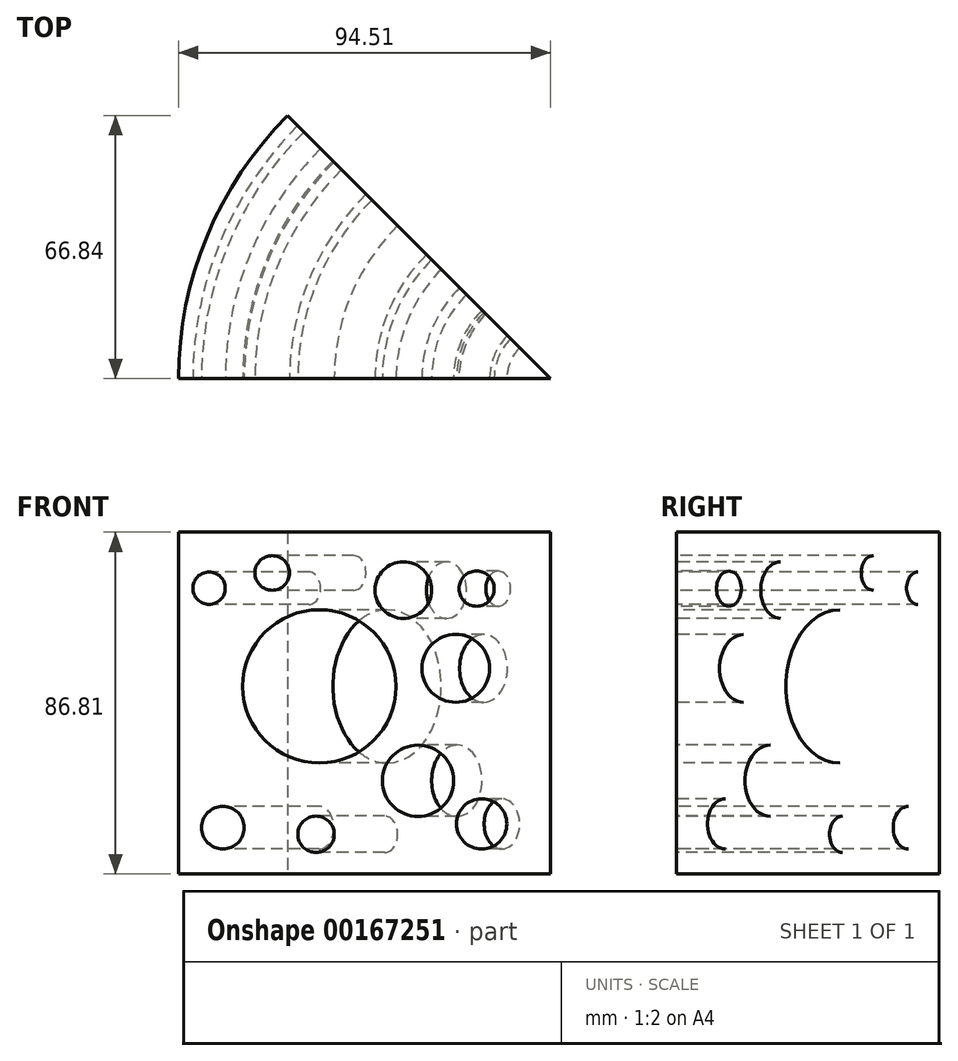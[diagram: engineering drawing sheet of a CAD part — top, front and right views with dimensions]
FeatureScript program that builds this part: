
annotation { "Feature Type Name" : "Feature", "Feature Type Description" : "" }
export const myFeature = defineFeature(function(context is Context, id is Id, definition is map)
    precondition{}
    {
        {
            var Q0;
            Q0=qCreatedBy(makeId("Front.planeOp"),FACE);
            var sketch = newSketch(context, id + "F0", { "sketchPlane" : qUnion([Q0])});
            skLineSegment(sketch, "E0.bottom", {"start": v(-65.07, 47.12) * mm, "end": v(29.44, 47.12) * mm});
            skLineSegment(sketch, "E0.top", {"start": v(-65.07, -39.69) * mm, "end": v(29.44, -39.69) * mm});
            skLineSegment(sketch, "E0.left", {"start": v(-65.07, 47.12) * mm, "end": v(-65.07, -39.69) * mm});
            skLineSegment(sketch, "E0.right", {"start": v(29.44, 47.12) * mm, "end": v(29.44, -39.69) * mm});
            skCircle(sketch, "E1", {"center": v(-29.3, 7.94) * mm, "radius": 19.48 * mm});
            skCircle(sketch, "E2", {"center": v(-53.81, -27.96) * mm, "radius": 5.41 * mm});
            skCircle(sketch, "E3", {"center": v(-30.15, -29.63) * mm, "radius": 4.63 * mm});
            skCircle(sketch, "E4", {"center": v(-4.24, -16.04) * mm, "radius": 9.06 * mm});
            skCircle(sketch, "E5", {"center": v(11.95, -27) * mm, "radius": 6.4 * mm});
            skCircle(sketch, "E6", {"center": v(5.35, 12.5) * mm, "radius": 8.62 * mm});
            skCircle(sketch, "E7", {"center": v(-7.97, 32.4) * mm, "radius": 7.2 * mm});
            skCircle(sketch, "E8", {"center": v(10.64, 32.78) * mm, "radius": 4.47 * mm});
            skCircle(sketch, "E9", {"center": v(-57.31, 32.9) * mm, "radius": 4.11 * mm});
            skCircle(sketch, "E10", {"center": v(-41.28, 36.77) * mm, "radius": 4.4 * mm});
            skSolve(sketch);
        }
        {
            var Q0;
            Q0=makeQuery(id+"F0.imprint","IMPRINT",FACE,{"disambiguationData":[TD([[makeQuery(id+"F0.imprint","IMPRINT",EDGE,{"derivedFrom":sQuery(id+"F0.wireOp",EDGE,"E0.bottom")}),-1.0]])]});
            var Q1;
            Q1=sQuery(id+"F0.wireOp",EDGE,"E0.right");
            revolve(context, id + "F1", {"surfaceOperationType" : NewSurfaceOperationType.NEW, "entities" : qUnion([Q0]), "axis" : qUnion([Q1]), "revolveType" : RevolveType.ONE_DIRECTION, "angle" : 45 * degree});
        }
    });
